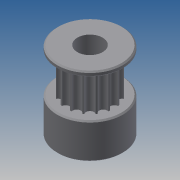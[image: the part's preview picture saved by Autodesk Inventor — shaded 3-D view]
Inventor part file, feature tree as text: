
AUTODESK INVENTOR PART (.ipt)
format: ipt  version: 2013 (Build 170138000, 138)  size: 162,304 bytes
history: native  units: mm
features: extrude x5, sketch x5, pattern_circular x1, chamfer x1
ambient origin geometry x8: Origin, YZ Plane, XZ Plane, XY Plane, X Axis, Y Axis, Z Axis, Center Point
bodies: Solid1 (feature_tree)
feature tree (12):
  extrude  "Extrusion1"  Depth=7.5mm TaperAngle=0.0deg
  extrude  "Extrusion2"  Depth=9.0mm TaperAngle=0.0deg
  pattern_circular  "Circular Pattern1"  Count=16 Angle=360.0deg
  extrude  "Extrusion3"  Depth=1.0mm TaperAngle=0.0deg
  extrude  "Extrusion4"  Depth=5.0mm
  extrude  "Extrusion5"  Depth=0.25mm TaperAngle=45.0deg
  chamfer  "Chamfer1"  [1 undecoded]
  sketch  "Sketch1"  dims[d0=9.683083mm d2=7.5mm d3=0.0mm]
  sketch  "Sketch2"  dims[d4=1.59mm d6=9.0mm d7=0.0mm d8=160.0mm d9=360.0deg]
  sketch  "Sketch3"  dims[d11=13.0mm d13=1.0mm d14=0.0mm]
  sketch  "Sketch4"  dims[d15=7.0mm d16=0.0mm d17=5.0mm]
  sketch  "Sketch5"  dims[d19=7.0mm d20=0.0mm d21=0.25mm d22=2.0mm d23=45.0deg]
note: 1 required parameter value undecoded (feature->parameter linkage not recoverable at this tier; creation-order binding heuristic only, values carry confidence <= 0.55)
